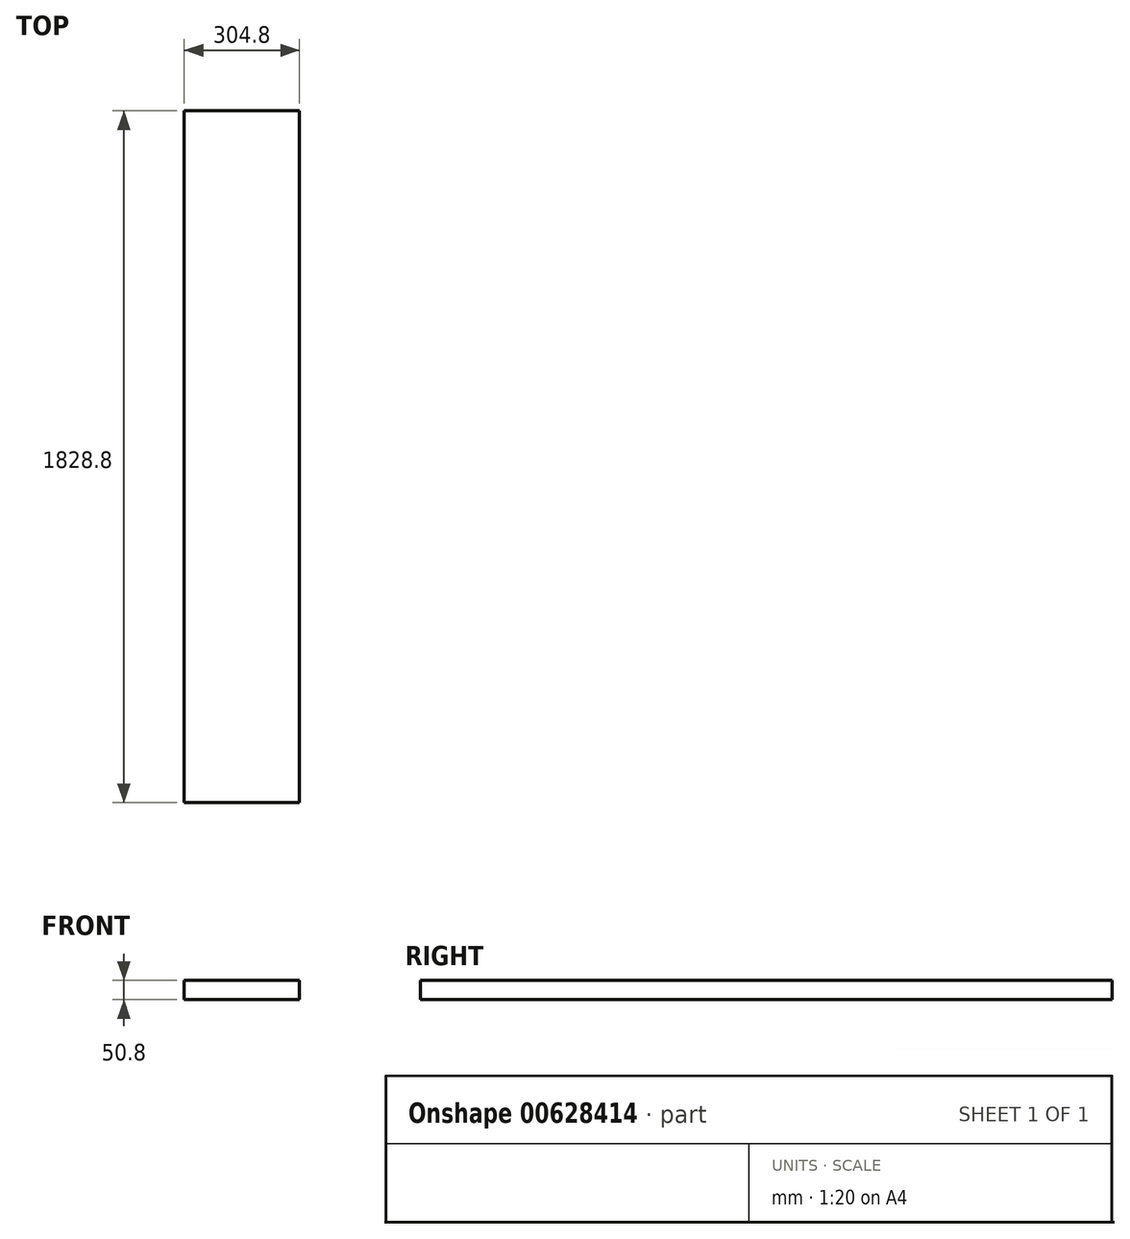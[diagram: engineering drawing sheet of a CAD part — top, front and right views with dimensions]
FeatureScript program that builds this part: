
annotation { "Feature Type Name" : "Feature", "Feature Type Description" : "" }
export const myFeature = defineFeature(function(context is Context, id is Id, definition is map)
    precondition{}
    {
        {
            var Q0;
            Q0=qCreatedBy(makeId("Front.planeOp"),FACE);
            var sketch = newSketch(context, id + "F0", { "sketchPlane" : qUnion([Q0])});
            skLineSegment(sketch, "E0", {"start": v(-152.4, 0) * mm, "end": v(152.4, 0) * mm});
            skLineSegment(sketch, "E1", {"start": v(152.4, 0) * mm, "end": v(152.4, 50.8) * mm});
            skLineSegment(sketch, "E2", {"start": v(152.4, 50.8) * mm, "end": v(-152.4, 50.8) * mm});
            skLineSegment(sketch, "E3", {"start": v(-152.4, 50.8) * mm, "end": v(-152.4, 0) * mm});
            skSolve(sketch);
        }
        {
            var Q0;
            Q0 = qSketchRegion(id + "F0", true);
            extrude(context, id + "F1", {"entities" : qUnion([Q0]), "depth" : 1828.8 * mm, "offsetDistance" : 25.4 * mm});
        }
    });
